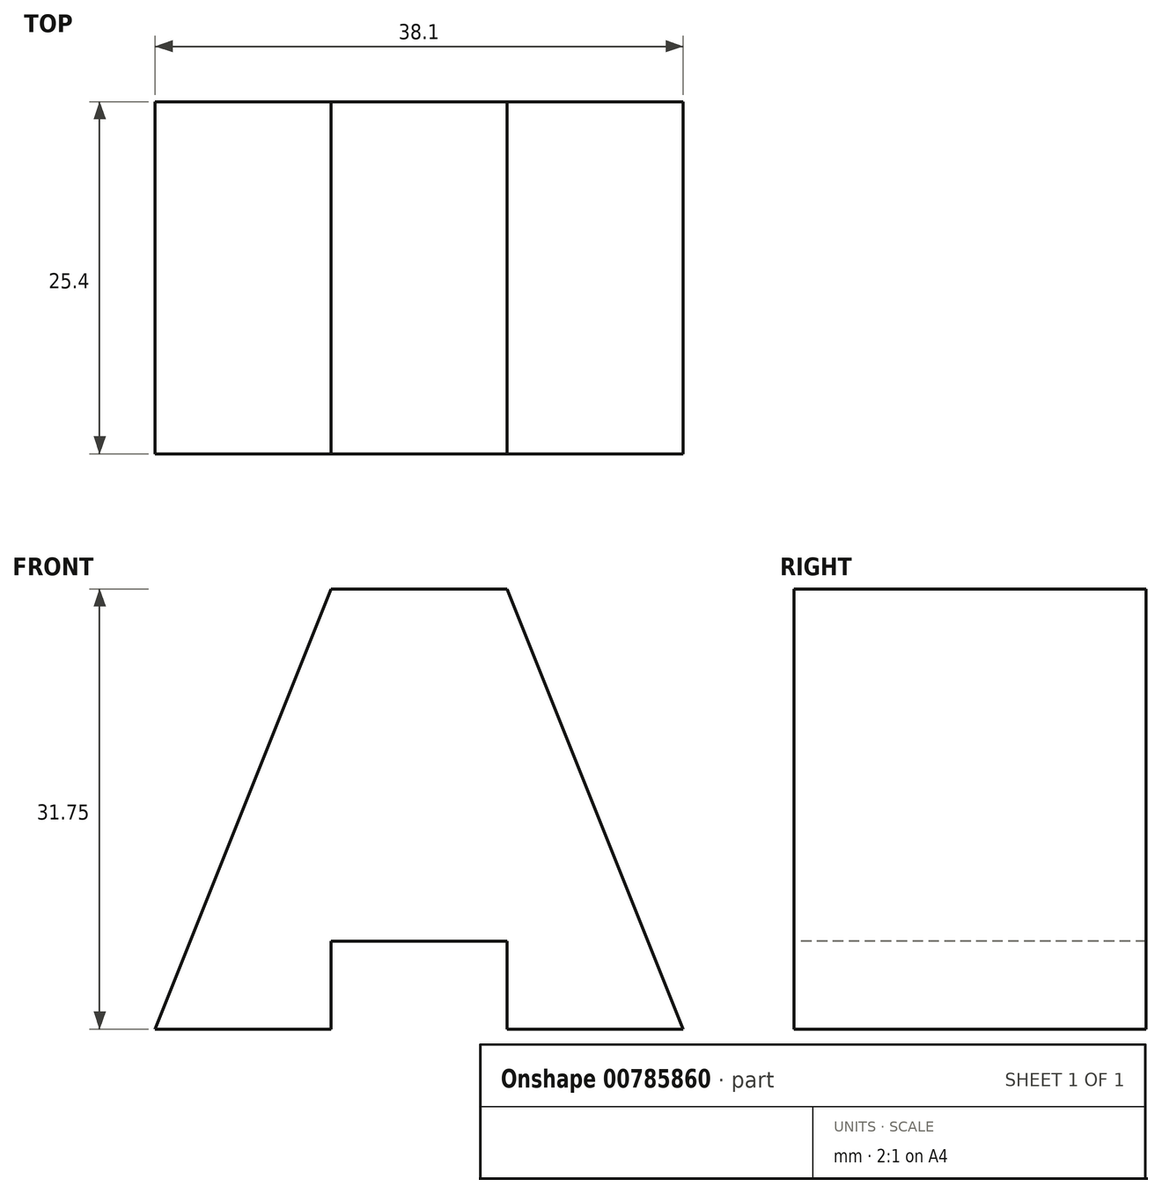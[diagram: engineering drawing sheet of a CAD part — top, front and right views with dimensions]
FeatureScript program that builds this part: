
annotation { "Feature Type Name" : "Feature", "Feature Type Description" : "" }
export const myFeature = defineFeature(function(context is Context, id is Id, definition is map)
    precondition{}
    {
        {
            var Q0;
            Q0=qCreatedBy(makeId("Front.planeOp"),FACE);
            var sketch = newSketch(context, id + "F0", { "sketchPlane" : qUnion([Q0])});
            skLineSegment(sketch, "E0", {"start": v(0, 0) * mm, "end": v(38.1, 0) * mm});
            skLineSegment(sketch, "E1", {"start": v(0, 0) * mm, "end": v(0, 31.75) * mm});
            skLineSegment(sketch, "E2", {"start": v(0, 31.75) * mm, "end": v(38.1, 31.75) * mm});
            skLineSegment(sketch, "E3", {"start": v(38.1, 0) * mm, "end": v(38.1, 31.75) * mm});
            skSolve(sketch);
        }
        {
            var Q0;
            Q0=makeQuery(id+"F0.imprint","IMPRINT",FACE,{"disambiguationData":[TD([[makeQuery(id+"F0.imprint","IMPRINT",EDGE,{"derivedFrom":sQuery(id+"F0.wireOp",EDGE,"E0")}),1.0]])]});
            extrude(context, id + "F1", {"entities" : qUnion([Q0]), "depth" : 25.4 * mm, "offsetDistance" : 25.4 * mm});
        }
        {
            var Q0;
            Q0=makeQuery(id+"F1.opExtrude","CAP_FACE",FACE,{"disambiguationData":[OSD([sQuery(id+"F0.wireOp",EDGE,"E0"),sQuery(id+"F0.wireOp",EDGE,"E1"),sQuery(id+"F0.wireOp",EDGE,"E2"),sQuery(id+"F0.wireOp",EDGE,"E3")])],"isStart":false});
            var sketch = newSketch(context, id + "F2", { "sketchPlane" : qUnion([Q0])});
            skLineSegment(sketch, "E4", {"start": v(0, 0) * mm, "end": v(12.7, 0) * mm});
            skLineSegment(sketch, "E5", {"start": v(38.1, 0) * mm, "end": v(25.4, 0) * mm});
            skLineSegment(sketch, "E6", {"start": v(12.7, 0) * mm, "end": v(12.7, 6.35) * mm});
            skLineSegment(sketch, "E7", {"start": v(12.7, 6.35) * mm, "end": v(25.4, 6.35) * mm});
            skLineSegment(sketch, "E8", {"start": v(25.4, 6.35) * mm, "end": v(25.4, 0) * mm});
            skSolve(sketch);
        }
        {
            var Q0;
            {var subQ0=sQuery(id+"F2.wireOp",EDGE,"E6");Q0=makeQuery(id+"F2.imprint","IMPRINT",FACE,{"disambiguationData":[TD([[makeQuery(id+"F2.imprint","IMPRINT",EDGE,{"derivedFrom":subQ0}),-1.0]])]});}
            extrude(context, id + "F3", {"entities" : qUnion([Q0]), "operationType" : NewBodyOperationType.REMOVE, "oppositeDirection" : true, "depth" : 25.4 * mm, "offsetDistance" : 25.4 * mm});
        }
        {
            var Q0;
            Q0=makeQuery(id+"F1.opExtrude","CAP_FACE",FACE,{"disambiguationData":[OSD([sQuery(id+"F0.wireOp",EDGE,"E0"),sQuery(id+"F0.wireOp",EDGE,"E1"),sQuery(id+"F0.wireOp",EDGE,"E2"),sQuery(id+"F0.wireOp",EDGE,"E3")])],"isStart":false});
            var sketch = newSketch(context, id + "F4", { "sketchPlane" : qUnion([Q0])});
            skLineSegment(sketch, "E9", {"start": v(0, 31.75) * mm, "end": v(12.7, 31.75) * mm});
            skLineSegment(sketch, "E10", {"start": v(38.1, 31.75) * mm, "end": v(25.4, 31.75) * mm});
            skLineSegment(sketch, "E11", {"start": v(0, 0) * mm, "end": v(12.7, 31.75) * mm});
            skLineSegment(sketch, "E12", {"start": v(25.4, 31.75) * mm, "end": v(38.1, 0) * mm});
            skSolve(sketch);
        }
        {
            var Q0;
            Q0=makeQuery(id+"F4.imprint","IMPRINT",FACE,{"disambiguationData":[TD([[makeQuery(id+"F4.imprint","IMPRINT",EDGE,{"derivedFrom":sQuery(id+"F4.wireOp",EDGE,"E10")}),-1.0]])]});
            extrude(context, id + "F5", {"entities" : qUnion([Q0]), "operationType" : NewBodyOperationType.REMOVE, "oppositeDirection" : true, "depth" : 25.4 * mm, "offsetDistance" : 25.4 * mm});
        }
        {
            var Q0;
            Q0=makeQuery(id+"F1.opExtrude","CAP_FACE",FACE,{"disambiguationData":[OSD([sQuery(id+"F0.wireOp",EDGE,"E0"),sQuery(id+"F0.wireOp",EDGE,"E1"),sQuery(id+"F0.wireOp",EDGE,"E2"),sQuery(id+"F0.wireOp",EDGE,"E3")])],"isStart":false});
            var sketch = newSketch(context, id + "F6", { "sketchPlane" : qUnion([Q0])});
            skLineSegment(sketch, "E13", {"start": v(0, 0) * mm, "end": v(12.7, 31.75) * mm});
            skSolve(sketch);
        }
        {
            var Q0;
            {var subQ0=sQuery(id+"F6.wireOp",EDGE,"E13");Q0=makeQuery(id+"F6.imprint","IMPRINT",FACE,{"disambiguationData":[TD([[makeQuery(id+"F6.imprint","IMPRINT",EDGE,{"derivedFrom":subQ0}),1.0]])]});}
            extrude(context, id + "F7", {"entities" : qUnion([Q0]), "operationType" : NewBodyOperationType.REMOVE, "oppositeDirection" : true, "depth" : 25.4 * mm, "offsetDistance" : 25.4 * mm});
        }
    });
